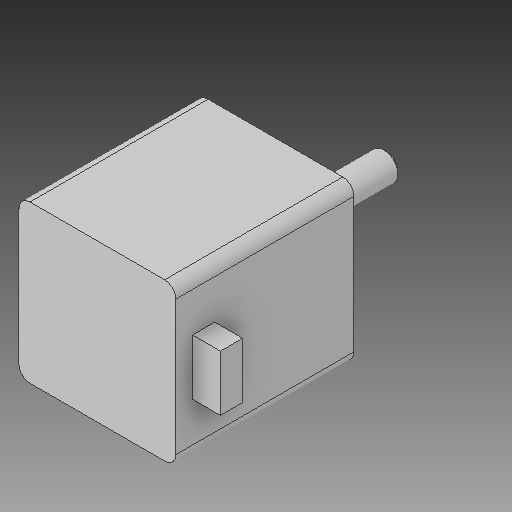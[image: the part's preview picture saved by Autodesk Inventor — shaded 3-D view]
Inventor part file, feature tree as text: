
AUTODESK INVENTOR PART (.ipt)
format: ipt  version: 2019 (Build 230136000, 136)  size: 137,216 bytes
history: native  units: mm
features: sketch x5, other x3
ambient origin geometry x8: Origin, YZ Plane, XZ Plane, XY Plane, X Axis, Y Axis, Z Axis, Center Point
bodies: Solid1 (feature_tree)
feature tree (8):
  other  "nema11.ipt"
  other  "Solid1::nema11.ipt"
  other  "TaggingFeature1"
  sketch  "Sketch1"  dims[d0=10.0mm]
  sketch  "Sketch2"
  sketch  "Sketch3"
  sketch  "Sketch4"
  sketch  "Sketch5"
